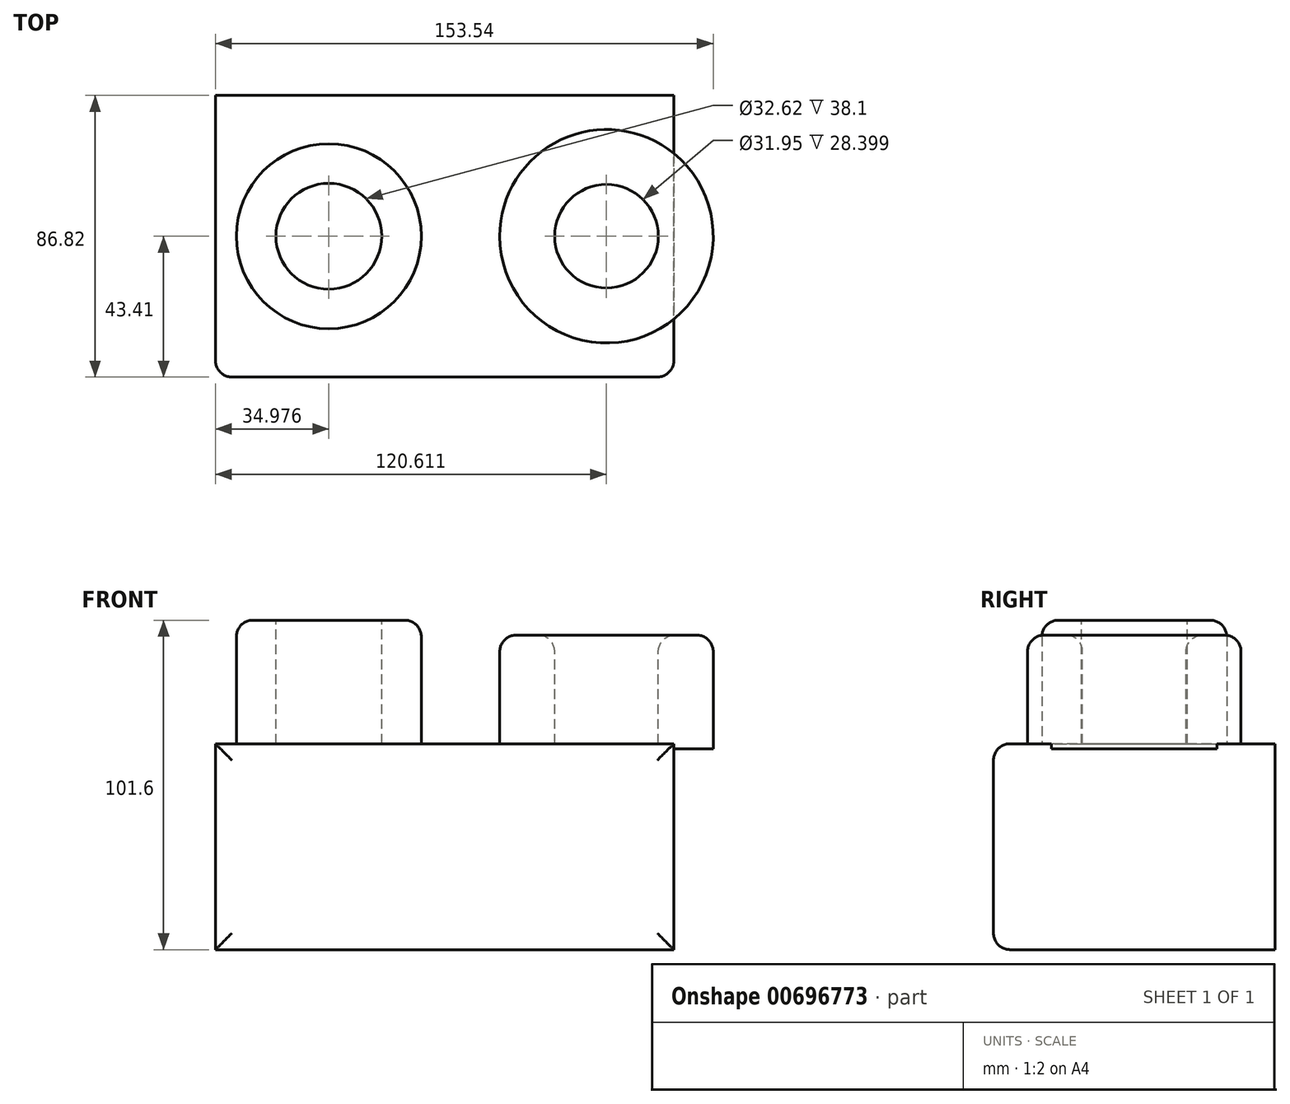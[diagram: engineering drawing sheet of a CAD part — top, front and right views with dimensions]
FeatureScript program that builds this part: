
annotation { "Feature Type Name" : "Feature", "Feature Type Description" : "" }
export const myFeature = defineFeature(function(context is Context, id is Id, definition is map)
    precondition{}
    {
        {
            var Q0;
            Q0=qCreatedBy(makeId("Top.planeOp"),FACE);
            var sketch = newSketch(context, id + "F0", { "sketchPlane" : qUnion([Q0])});
            skLineSegment(sketch, "E0.bottom", {"start": v(70.7, -43.4) * mm, "end": v(-70.7, -43.4) * mm});
            skLineSegment(sketch, "E0.top", {"start": v(70.7, 43.4) * mm, "end": v(-70.7, 43.4) * mm});
            skLineSegment(sketch, "E0.left", {"start": v(70.7, -43.4) * mm, "end": v(70.7, 43.4) * mm});
            skLineSegment(sketch, "E0.right", {"start": v(-70.7, -43.4) * mm, "end": v(-70.7, 43.4) * mm});
            skPoint(sketch, "E0.middle", {"position": v(0, 0) * mm});
            skSolve(sketch);
        }
        {
            var Q0;
            Q0=makeQuery(id+"F0.imprint","IMPRINT",FACE,{"disambiguationData":[TD([[makeQuery(id+"F0.imprint","IMPRINT",EDGE,{"derivedFrom":sQuery(id+"F0.wireOp",EDGE,"E0.bottom")}),-1.0]])]});
            extrude(context, id + "F1", {"entities" : qUnion([Q0]), "depth" : 63.5 * mm, "offsetDistance" : 25.4 * mm});
        }
        {
            var Q0;
            Q0=makeQuery(id+"F1.opExtrude","CAP_FACE",FACE,{"disambiguationData":[OSD([sQuery(id+"F0.wireOp",EDGE,"E0.bottom"),sQuery(id+"F0.wireOp",EDGE,"E0.top"),sQuery(id+"F0.wireOp",EDGE,"E0.left"),sQuery(id+"F0.wireOp",EDGE,"E0.right")])],"isStart":false});
            var sketch = newSketch(context, id + "F2", { "sketchPlane" : qUnion([Q0])});
            skCircle(sketch, "E1", {"center": v(-35.71, 0) * mm, "radius": 28.51 * mm});
            skSolve(sketch);
        }
        {
            var Q0;
            Q0=makeQuery(id+"F2.imprint","IMPRINT",FACE,{"disambiguationData":[TD([[makeQuery(id+"F2.imprint","IMPRINT",EDGE,{"derivedFrom":sQuery(id+"F2.wireOp",EDGE,"E1")}),1.0]])]});
            extrude(context, id + "F3", {"entities" : qUnion([Q0]), "operationType" : NewBodyOperationType.ADD, "depth" : 38.1 * mm, "offsetDistance" : 25.4 * mm});
        }
        {
            var Q0;
            Q0=makeQuery(id+"F3.opExtrude","CAP_FACE",FACE,{"disambiguationData":[OSD([sQuery(id+"F2.wireOp",EDGE,"E1")])],"isStart":false});
            var sketch = newSketch(context, id + "F4", { "sketchPlane" : qUnion([Q0])});
            skCircle(sketch, "E2", {"center": v(-35.71, 0) * mm, "radius": 16.3 * mm});
            skSolve(sketch);
        }
        {
            var Q0;
            Q0=makeQuery(id+"F4.imprint","IMPRINT",FACE,{"disambiguationData":[TD([[makeQuery(id+"F4.imprint","IMPRINT",EDGE,{"derivedFrom":sQuery(id+"F4.wireOp",EDGE,"E2")}),1.0]])]});
            var Q1;
            Q1=makeQuery(id+"F1.opExtrude","CAP_FACE",FACE,{"disambiguationData":[OSD([sQuery(id+"F0.wireOp",EDGE,"E0.bottom"),sQuery(id+"F0.wireOp",EDGE,"E0.top"),sQuery(id+"F0.wireOp",EDGE,"E0.left"),sQuery(id+"F0.wireOp",EDGE,"E0.right")])],"isStart":false});
            extrude(context, id + "F5", {"entities" : qUnion([Q0]), "operationType" : NewBodyOperationType.REMOVE, "endBound" : BoundingType.UP_TO_SURFACE, "oppositeDirection" : true, "depth" : 25.4 * mm, "endBoundEntityFace" : qUnion([Q1]), "offsetDistance" : 25.4 * mm});
        }
        {
            var Q0;
            Q0=qCreatedBy(makeId("Front.planeOp"),FACE);
            var sketch = newSketch(context, id + "F6", { "sketchPlane" : qUnion([Q0])});
            skLineSegment(sketch, "E3", {"start": v(49.92, 93.85) * mm, "end": v(49.92, 34.1) * mm});
            skLineSegment(sketch, "E4.bottom", {"start": v(17, 96.98) * mm, "end": v(33.95, 96.98) * mm});
            skLineSegment(sketch, "E4.top", {"start": v(17, 61.9) * mm, "end": v(33.95, 61.9) * mm});
            skLineSegment(sketch, "E4.left", {"start": v(17, 96.98) * mm, "end": v(17, 61.9) * mm});
            skLineSegment(sketch, "E4.right", {"start": v(33.95, 96.98) * mm, "end": v(33.95, 61.9) * mm});
            skSolve(sketch);
        }
        {
            var Q0;
            Q0=makeQuery(id+"F6.imprint","IMPRINT",FACE,{"disambiguationData":[TD([[makeQuery(id+"F6.imprint","IMPRINT",EDGE,{"derivedFrom":sQuery(id+"F6.wireOp",EDGE,"E4.bottom")}),-1.0]])]});
            var Q1;
            Q1=sQuery(id+"F6.wireOp",EDGE,"E3");
            revolve(context, id + "F7", {"operationType" : NewBodyOperationType.ADD, "entities" : qUnion([Q0]), "axis" : qUnion([Q1]), "revolveType" : RevolveType.FULL});
        }
        {
            var Q0;
            Q0=makeQuery(id+"F7.opRevolve","SWEPT_EDGE",EDGE,{"disambiguationData":[OSD([sQuery(id+"F6.wireOp",EDGE,"E4.bottom"),sQuery(id+"F6.wireOp",EDGE,"E4.left")])]});
            var Q1;
            Q1=makeQuery(id+"F3.opExtrude","CAP_EDGE",EDGE,{"disambiguationData":[OSD([sQuery(id+"F2.wireOp",EDGE,"E1")])],"isStart":false});
            var Q2;
            Q2=makeQuery(id+"F7.opRevolve","SWEPT_EDGE",EDGE,{"disambiguationData":[OSD([sQuery(id+"F6.wireOp",EDGE,"E4.bottom"),sQuery(id+"F6.wireOp",EDGE,"E4.right")])]});
            var Q3;
            Q3=makeQuery(id+"F1.opExtrude","CAP_EDGE",EDGE,{"disambiguationData":[OSD([sQuery(id+"F0.wireOp",EDGE,"E0.bottom")])],"isStart":false});
            var Q4;
            Q4=makeQuery(id+"F1.opExtrude","SWEPT_EDGE",EDGE,{"disambiguationData":[OSD([sQuery(id+"F0.wireOp",EDGE,"E0.bottom"),sQuery(id+"F0.wireOp",EDGE,"E0.left")])]});
            var Q5;
            Q5=makeQuery(id+"F1.opExtrude","SWEPT_EDGE",EDGE,{"disambiguationData":[OSD([sQuery(id+"F0.wireOp",EDGE,"E0.bottom"),sQuery(id+"F0.wireOp",EDGE,"E0.right")])]});
            var Q6;
            Q6=makeQuery(id+"F1.opExtrude","CAP_EDGE",EDGE,{"disambiguationData":[OSD([sQuery(id+"F0.wireOp",EDGE,"E0.bottom")])],"isStart":true});
            var Q7;
            Q7=makeQuery(id+"F5.boolean.opBoolean","COPY",EDGE,{"derivedFrom":makeQuery(id+"F5.opExtrude","CAP_EDGE",EDGE,{"disambiguationData":[OSD([sQuery(id+"F4.wireOp",EDGE,"E2")])],"isStart":true})});
            fillet(context, id + "F8", {"entities" : qUnion([Q0, Q1, Q2, Q3, Q4, Q5, Q6, Q7]), "radius" : 5.08 * mm, "tangentPropagation" : true, "allowEdgeOverflow" : false});
        }
    });
